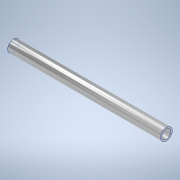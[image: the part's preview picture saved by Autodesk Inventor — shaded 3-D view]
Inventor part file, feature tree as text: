
AUTODESK INVENTOR PART (.ipt)
format: ipt  version: 2020.3 (Build 243373000, 373)  size: 101,376 bytes
history: native  units: mm
features: other x1, extrude x1, sketch x1
ambient origin geometry x8: Origin, YZ Plane, XZ Plane, XY Plane, X Axis, Y Axis, Z Axis, Center Point
bodies: Body1 (feature_tree)
feature tree (3):
  other  "ソリッド1"
  extrude  "押し出し1"  Depth=4.0mm
  sketch  "スケッチ1"
